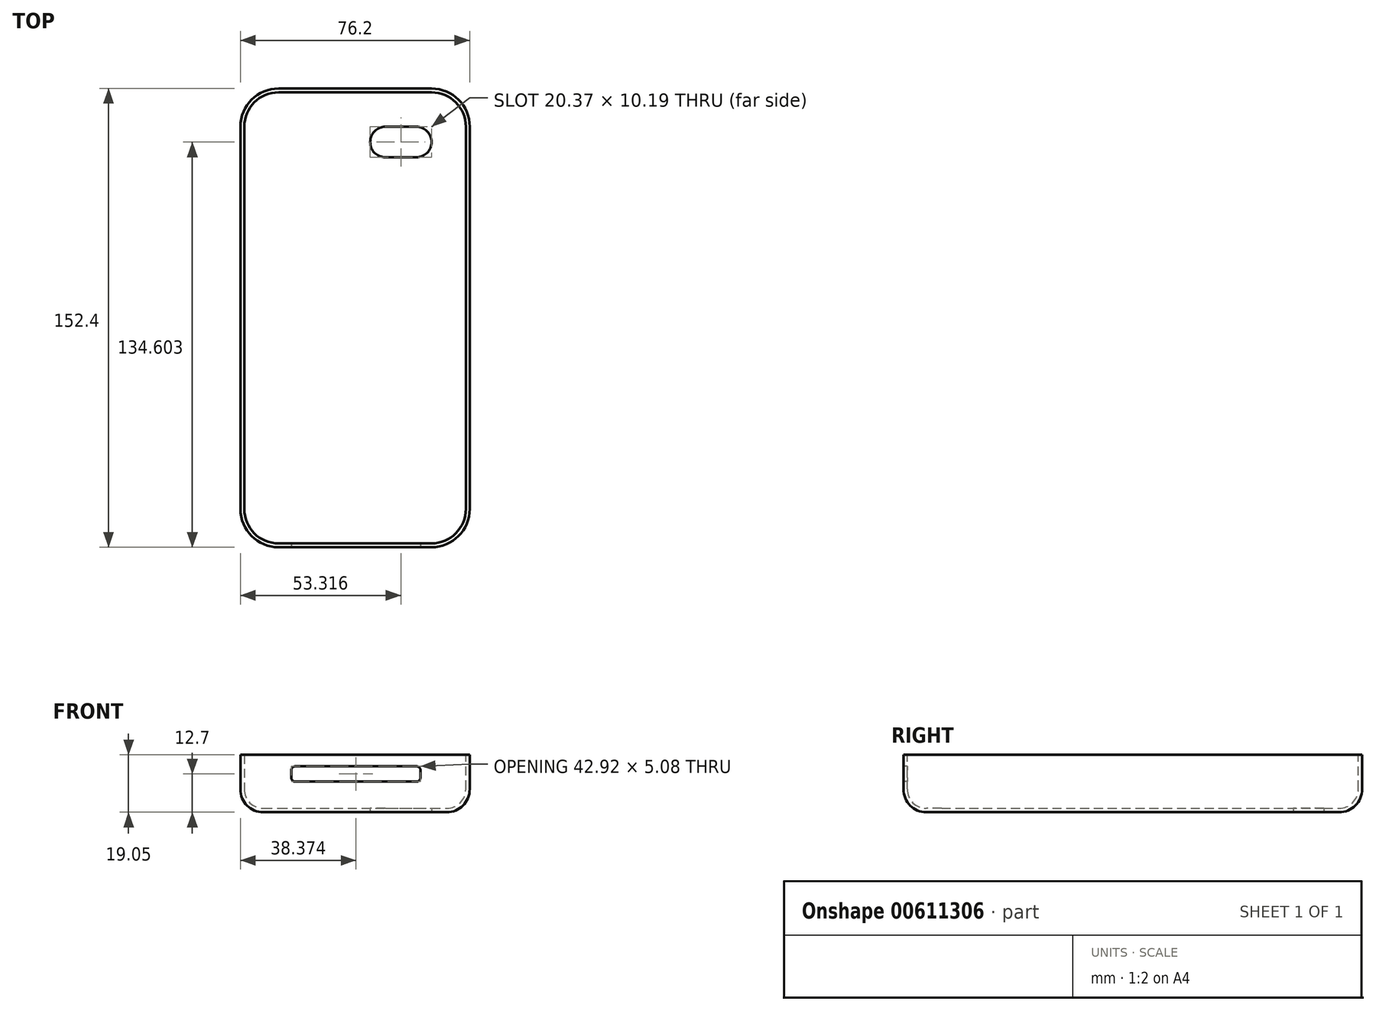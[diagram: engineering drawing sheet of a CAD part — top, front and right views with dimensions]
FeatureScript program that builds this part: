
annotation { "Feature Type Name" : "Feature", "Feature Type Description" : "" }
export const myFeature = defineFeature(function(context is Context, id is Id, definition is map)
    precondition{}
    {
        {
            var Q0;
            Q0=qCreatedBy(makeId("Top.planeOp"),FACE);
            var sketch = newSketch(context, id + "F0", { "sketchPlane" : qUnion([Q0])});
            skLineSegment(sketch, "E0.bottom", {"start": v(-50.2, 85.07) * mm, "end": v(26, 85.07) * mm});
            skLineSegment(sketch, "E0.top", {"start": v(-50.2, -67.33) * mm, "end": v(26, -67.33) * mm});
            skLineSegment(sketch, "E0.left", {"start": v(-50.2, 85.07) * mm, "end": v(-50.2, -67.33) * mm});
            skLineSegment(sketch, "E0.right", {"start": v(26, 85.07) * mm, "end": v(26, -67.33) * mm});
            skSolve(sketch);
        }
        {
            var Q0;
            Q0=makeQuery(id+"F0.imprint","IMPRINT",FACE,{"disambiguationData":[TD([[makeQuery(id+"F0.imprint","IMPRINT",EDGE,{"derivedFrom":sQuery(id+"F0.wireOp",EDGE,"E0.bottom")}),-1.0]])]});
            extrude(context, id + "F1", {"entities" : qUnion([Q0]), "depth" : 19.05 * mm, "offsetDistance" : 25.4 * mm});
        }
        {
            var Q0;
            Q0=makeQuery(id+"F1.opExtrude","SWEPT_EDGE",EDGE,{"disambiguationData":[OSD([sQuery(id+"F0.wireOp",EDGE,"E0.bottom"),sQuery(id+"F0.wireOp",EDGE,"E0.right")])]});
            var Q1;
            Q1=makeQuery(id+"F1.opExtrude","SWEPT_EDGE",EDGE,{"disambiguationData":[OSD([sQuery(id+"F0.wireOp",EDGE,"E0.top"),sQuery(id+"F0.wireOp",EDGE,"E0.right")])]});
            var Q2;
            Q2=makeQuery(id+"F1.opExtrude","SWEPT_EDGE",EDGE,{"disambiguationData":[OSD([sQuery(id+"F0.wireOp",EDGE,"E0.bottom"),sQuery(id+"F0.wireOp",EDGE,"E0.left")])]});
            var Q3;
            Q3=makeQuery(id+"F1.opExtrude","SWEPT_EDGE",EDGE,{"disambiguationData":[OSD([sQuery(id+"F0.wireOp",EDGE,"E0.top"),sQuery(id+"F0.wireOp",EDGE,"E0.left")])]});
            fillet(context, id + "F2", {"entities" : qUnion([Q0, Q1, Q2, Q3]), "radius" : 12.7 * mm, "tangentPropagation" : true, "allowEdgeOverflow" : false});
        }
        {
            var Q0;
            Q0=makeQuery(id+"F1.opExtrude","CAP_FACE",FACE,{"disambiguationData":[OSD([sQuery(id+"F0.wireOp",EDGE,"E0.bottom"),sQuery(id+"F0.wireOp",EDGE,"E0.top"),sQuery(id+"F0.wireOp",EDGE,"E0.left"),sQuery(id+"F0.wireOp",EDGE,"E0.right")])],"isStart":true});
            fillet(context, id + "F3", {"entities" : qUnion([Q0]), "radius" : 7.62 * mm, "tangentPropagation" : true, "allowEdgeOverflow" : false});
        }
        {
            var Q0;
            Q0=makeQuery(id+"F1.opExtrude","CAP_FACE",FACE,{"disambiguationData":[OSD([sQuery(id+"F0.wireOp",EDGE,"E0.bottom"),sQuery(id+"F0.wireOp",EDGE,"E0.top"),sQuery(id+"F0.wireOp",EDGE,"E0.left"),sQuery(id+"F0.wireOp",EDGE,"E0.right")])],"isStart":false});
            shell(context, id + "F4", {"entities" : qUnion([Q0]), "thickness" : 1.27 * mm});
        }
        {
            var Q0;
            Q0=makeQuery(id+"F1.opExtrude","CAP_FACE",FACE,{"disambiguationData":[OSD([sQuery(id+"F0.wireOp",EDGE,"E0.bottom"),sQuery(id+"F0.wireOp",EDGE,"E0.top"),sQuery(id+"F0.wireOp",EDGE,"E0.left"),sQuery(id+"F0.wireOp",EDGE,"E0.right")])],"isStart":true});
            var sketch = newSketch(context, id + "F5", { "sketchPlane" : qUnion([Q0])});
            skArc(sketch, "E1", {"start": v(8.2, -72.37) * mm, "mid": v(13.3, -67.27) * mm, "end": v(8.2, -62.18) * mm});
            skArc(sketch, "E2", {"start": v(-1.99, -62.18) * mm, "mid": v(-7.08, -67.27) * mm, "end": v(-1.99, -72.37) * mm});
            skLineSegment(sketch, "E3", {"start": v(8.2, -72.37) * mm, "end": v(-1.99, -72.37) * mm});
            skLineSegment(sketch, "E4", {"start": v(8.2, -62.18) * mm, "end": v(-1.99, -62.18) * mm});
            skSolve(sketch);
        }
        {
            var Q0;
            Q0=makeQuery(id+"F5.imprint","IMPRINT",FACE,{"disambiguationData":[TD([[makeQuery(id+"F5.imprint","IMPRINT",EDGE,{"derivedFrom":sQuery(id+"F5.wireOp",EDGE,"E1")}),1.0]])]});
            extrude(context, id + "F6", {"entities" : qUnion([Q0]), "operationType" : NewBodyOperationType.REMOVE, "oppositeDirection" : true, "depth" : 25.4 * mm, "offsetDistance" : 25.4 * mm});
        }
        {
            var Q0;
            Q0=makeQuery(id+"F1.opExtrude","SWEPT_FACE",FACE,{"disambiguationData":[OSD([sQuery(id+"F0.wireOp",EDGE,"E0.top")])]});
            var sketch = newSketch(context, id + "F7", { "sketchPlane" : qUnion([Q0])});
            skLineSegment(sketch, "E5.bottom", {"start": v(-32.03, 15.24) * mm, "end": v(8.36, 15.24) * mm});
            skLineSegment(sketch, "E5.top", {"start": v(-32.03, 10.16) * mm, "end": v(8.36, 10.16) * mm});
            skLineSegment(sketch, "E5.left", {"start": v(-33.3, 13.97) * mm, "end": v(-33.3, 11.43) * mm});
            skLineSegment(sketch, "E5.right", {"start": v(9.63, 13.97) * mm, "end": v(9.63, 11.43) * mm});
            skPoint(sketch, "E6.visualSharp", {"position": v(-33.3, 15.24) * mm});
            skArc(sketch, "E6.filletArc", {"start": v(-32.03, 15.24) * mm, "mid": v(-32.93, 14.87) * mm, "end": v(-33.3, 13.97) * mm});
            skPoint(sketch, "E7.visualSharp", {"position": v(9.63, 15.24) * mm});
            skArc(sketch, "E7.filletArc", {"start": v(9.63, 13.97) * mm, "mid": v(9.25, 14.87) * mm, "end": v(8.36, 15.24) * mm});
            skPoint(sketch, "E8.visualSharp", {"position": v(9.63, 10.16) * mm});
            skArc(sketch, "E8.filletArc", {"start": v(8.36, 10.16) * mm, "mid": v(9.25, 10.53) * mm, "end": v(9.63, 11.43) * mm});
            skPoint(sketch, "E9.visualSharp", {"position": v(-33.3, 10.16) * mm});
            skArc(sketch, "E9.filletArc", {"start": v(-33.3, 11.43) * mm, "mid": v(-32.93, 10.53) * mm, "end": v(-32.03, 10.16) * mm});
            skSolve(sketch);
        }
        {
            var Q0;
            Q0=makeQuery(id+"F7.imprint","IMPRINT",FACE,{"disambiguationData":[TD([[makeQuery(id+"F7.imprint","IMPRINT",EDGE,{"derivedFrom":sQuery(id+"F7.wireOp",EDGE,"E5.bottom")}),-1.0]])]});
            extrude(context, id + "F8", {"entities" : qUnion([Q0]), "operationType" : NewBodyOperationType.REMOVE, "oppositeDirection" : true, "depth" : 25.4 * mm, "offsetDistance" : 25.4 * mm});
        }
    });
